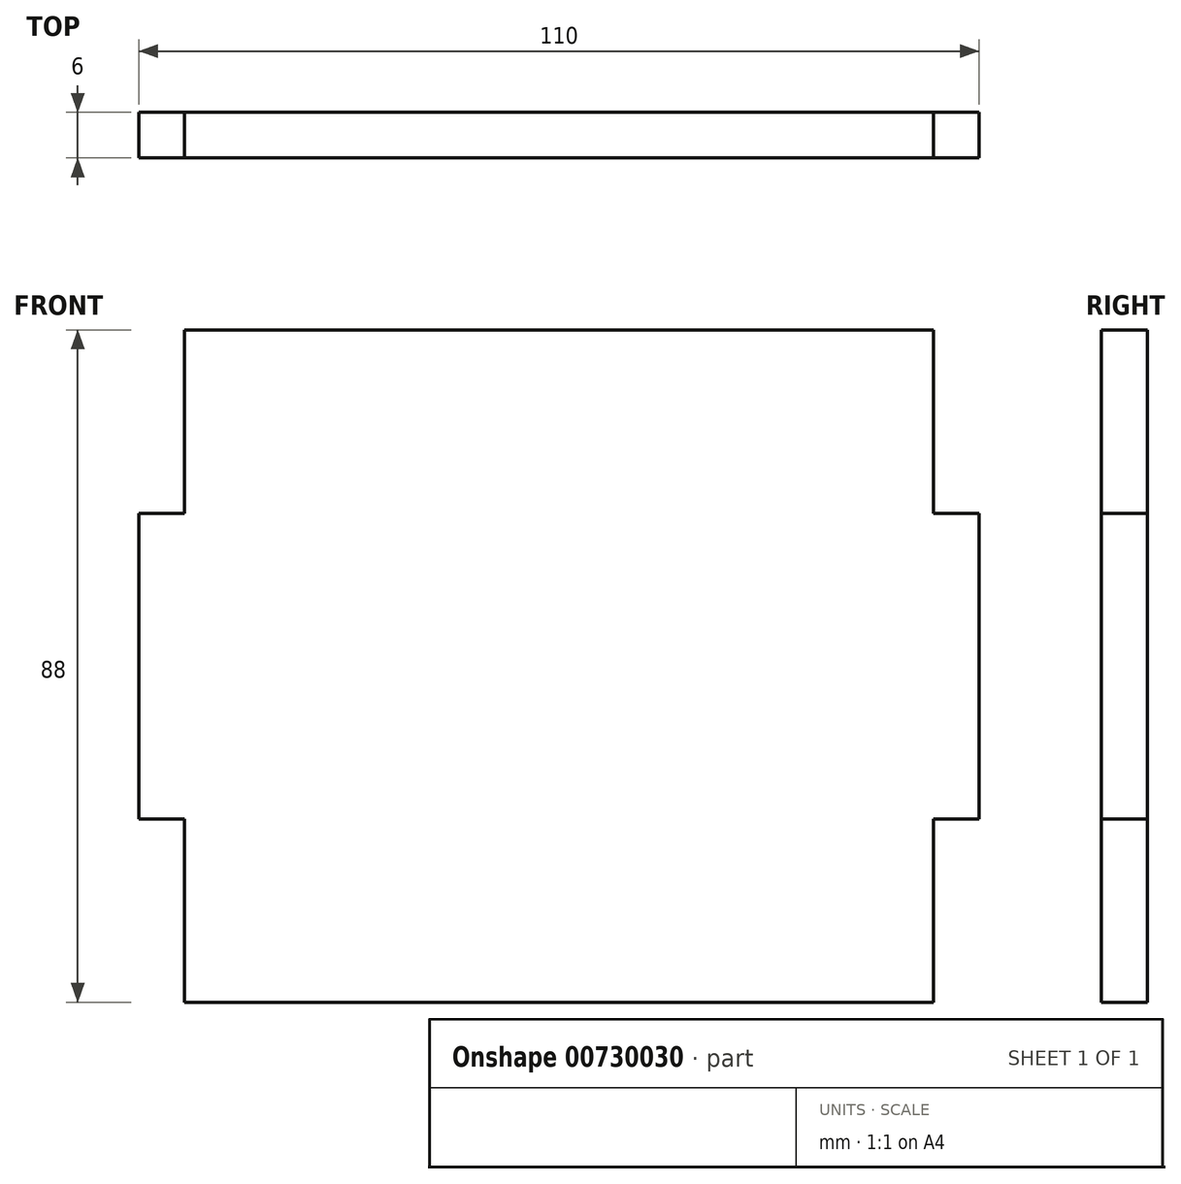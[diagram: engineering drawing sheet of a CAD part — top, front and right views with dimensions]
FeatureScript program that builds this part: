
annotation { "Feature Type Name" : "Feature", "Feature Type Description" : "" }
export const myFeature = defineFeature(function(context is Context, id is Id, definition is map)
    precondition{}
    {
        {
            var Q0;
            Q0=qCreatedBy(makeId("Front.planeOp"),FACE);
            var sketch = newSketch(context, id + "F0", { "sketchPlane" : qUnion([Q0])});
            skLineSegment(sketch, "E0", {"start": v(-62.9, -46.68) * mm, "end": v(35.1, -46.68) * mm});
            skLineSegment(sketch, "E1", {"start": v(35.1, -46.68) * mm, "end": v(35.1, -22.68) * mm});
            skLineSegment(sketch, "E2", {"start": v(35.1, -22.68) * mm, "end": v(41.1, -22.68) * mm});
            skLineSegment(sketch, "E3", {"start": v(41.1, -22.68) * mm, "end": v(41.1, 17.32) * mm});
            skLineSegment(sketch, "E4", {"start": v(41.1, 17.32) * mm, "end": v(35.1, 17.32) * mm});
            skLineSegment(sketch, "E5", {"start": v(35.1, 17.32) * mm, "end": v(35.1, 41.32) * mm});
            skLineSegment(sketch, "E6", {"start": v(35.1, 41.32) * mm, "end": v(-62.9, 41.32) * mm});
            skLineSegment(sketch, "E7", {"start": v(-62.9, 41.32) * mm, "end": v(-62.9, 17.32) * mm});
            skLineSegment(sketch, "E8", {"start": v(-62.9, 17.32) * mm, "end": v(-68.9, 17.32) * mm});
            skLineSegment(sketch, "E9", {"start": v(-68.9, 17.32) * mm, "end": v(-68.9, -22.68) * mm});
            skLineSegment(sketch, "E10", {"start": v(-68.9, -22.68) * mm, "end": v(-62.9, -22.68) * mm});
            skLineSegment(sketch, "E11", {"start": v(-62.9, -22.68) * mm, "end": v(-62.9, -46.68) * mm});
            skSolve(sketch);
        }
        {
            var Q0;
            Q0 = qSketchRegion(id + "F0", true);
            extrude(context, id + "F1", {"entities" : qUnion([Q0]), "depth" : 6 * mm, "offsetDistance" : 25 * mm});
        }
    });
